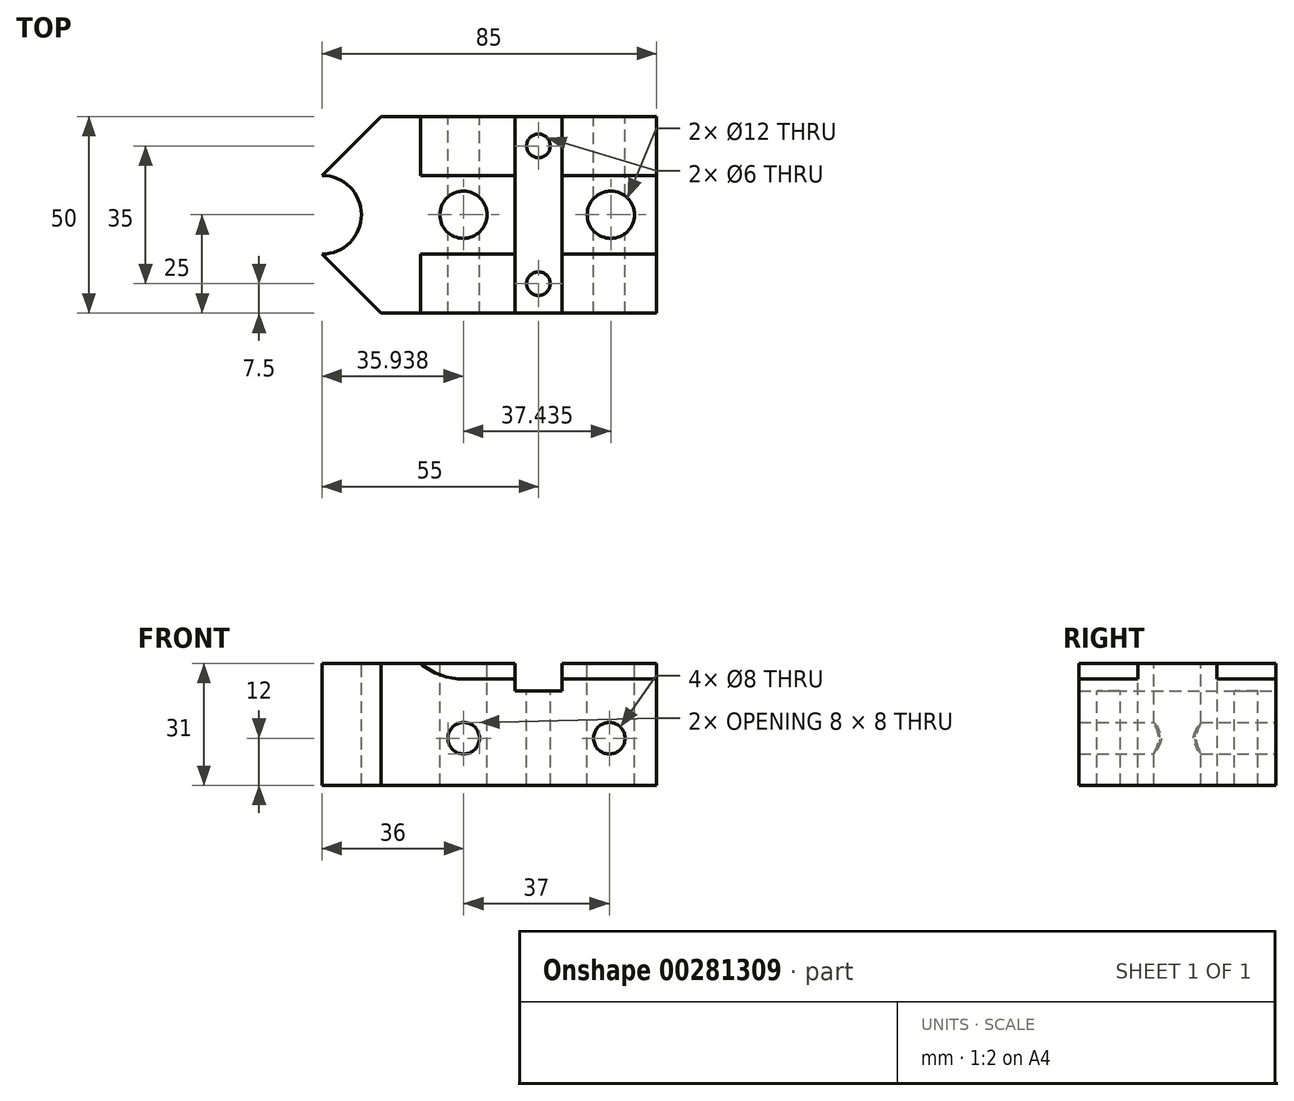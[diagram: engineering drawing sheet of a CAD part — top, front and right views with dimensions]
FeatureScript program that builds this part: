
annotation { "Feature Type Name" : "Feature", "Feature Type Description" : "" }
export const myFeature = defineFeature(function(context is Context, id is Id, definition is map)
    precondition{}
    {
        {
            var Q0;
            Q0=qCreatedBy(makeId("Front.planeOp"),FACE);
            var sketch = newSketch(context, id + "F0", { "sketchPlane" : qUnion([Q0])});
            skLineSegment(sketch, "E0", {"start": v(35, 0) * mm, "end": v(35, 27) * mm});
            skLineSegment(sketch, "E1", {"start": v(35, 27) * mm, "end": v(11, 27) * mm});
            skLineSegment(sketch, "E2", {"start": v(11, 27) * mm, "end": v(11, 24) * mm});
            skLineSegment(sketch, "E3", {"start": v(11, 24) * mm, "end": v(-1, 24) * mm});
            skLineSegment(sketch, "E4", {"start": v(-1, 24) * mm, "end": v(-1, 27) * mm});
            skLineSegment(sketch, "E5", {"start": v(-1, 27) * mm, "end": v(-14, 27) * mm});
            skArc(sketch, "E6", {"start": v(-14, 27) * mm, "mid": v(-19.85, 28.03) * mm, "end": v(-25, 31) * mm});
            skLineSegment(sketch, "E7", {"start": v(-25, 31) * mm, "end": v(-1, 31) * mm});
            skLineSegment(sketch, "E8", {"start": v(-1, 27) * mm, "end": v(-1, 31) * mm});
            skPoint(sketch, "E9.start.orphan", {"position": v(-35, 0) * mm});
            skLineSegment(sketch, "E10", {"start": v(-25, 31) * mm, "end": v(-50, 31) * mm});
            skLineSegment(sketch, "E11", {"start": v(-50, 31) * mm, "end": v(-50, 0) * mm});
            skLineSegment(sketch, "E12", {"start": v(35, 0) * mm, "end": v(-50, 0) * mm});
            skPoint(sketch, "E13.endSnap0", {"position": v(23, 27) * mm});
            skPoint(sketch, "E14.end.orphan", {"position": v(35, 12) * mm});
            skCircle(sketch, "E15", {"center": v(23, 12) * mm, "radius": 4 * mm});
            skCircle(sketch, "E16", {"center": v(-14, 12) * mm, "radius": 4 * mm});
            skSolve(sketch);
        }
        {
            var Q0;
            Q0=makeQuery(id+"F0.imprint","IMPRINT",FACE,{"disambiguationData":[TD([[makeQuery(id+"F0.imprint","IMPRINT",EDGE,{"derivedFrom":sQuery(id+"F0.wireOp",EDGE,"E0")}),1.0]])]});
            extrude(context, id + "F1", {"entities" : qUnion([Q0]), "endBound" : BoundingType.SYMMETRIC, "depth" : 50 * mm});
        }
        {
            var Q0;
            Q0=makeQuery(id+"F0.imprint","IMPRINT",FACE,{"disambiguationData":[TD([[makeQuery(id+"F0.imprint","IMPRINT",EDGE,{"derivedFrom":sQuery(id+"F0.wireOp",EDGE,"E5")}),-1.0]])]});
            extrude(context, id + "F2", {"entities" : qUnion([Q0]), "operationType" : NewBodyOperationType.ADD, "endBound" : BoundingType.SYMMETRIC, "depth" : 20 * mm});
        }
        {
            var Q0;
            Q0=makeQuery(id+"F1.opExtrude","CAP_EDGE",EDGE,{"disambiguationData":[OSD([sQuery(id+"F0.wireOp",EDGE,"E11")])],"isStart":false});
            var Q1;
            Q1=makeQuery(id+"F1.opExtrude","CAP_EDGE",EDGE,{"disambiguationData":[OSD([sQuery(id+"F0.wireOp",EDGE,"E11")])],"isStart":true});
            chamfer(context, id + "F3", {"entities" : qUnion([Q0, Q1]), "width" : 15 * mm, "tangentPropagation" : true});
        }
        {
            var Q0;
            Q0=makeQuery(id+"F2.boolean.opBoolean","MERGE",FACE,{"derivedFrom":[makeQuery(id+"F1.opExtrude","SWEPT_FACE",FACE,{"disambiguationData":[OSD([sQuery(id+"F0.wireOp",EDGE,"E10")])]}),makeQuery(id+"F2.opExtrude","SWEPT_FACE",FACE,{"disambiguationData":[OSD([sQuery(id+"F0.wireOp",EDGE,"E7")])]})]});
            var sketch = newSketch(context, id + "F4", { "sketchPlane" : qUnion([Q0])});
            skCircle(sketch, "E17", {"center": v(-50, 0) * mm, "radius": 10 * mm});
            skSolve(sketch);
        }
        {
            var Q0;
            Q0 = qSketchRegion(id + "F4", true);
            extrude(context, id + "F5", {"entities" : qUnion([Q0]), "operationType" : NewBodyOperationType.REMOVE, "oppositeDirection" : true, "depth" : 31 * mm});
        }
        {
            var Q0;
            Q0=makeQuery(id+"F1.opExtrude","SWEPT_FACE",FACE,{"disambiguationData":[OSD([sQuery(id+"F0.wireOp",EDGE,"E0")])]});
            var sketch = newSketch(context, id + "F6", { "sketchPlane" : qUnion([Q0])});
            skLineSegment(sketch, "E18", {"start": v(-10, 27) * mm, "end": v(-10, 31) * mm});
            skLineSegment(sketch, "E19", {"start": v(-10, 31) * mm, "end": v(10, 31) * mm});
            skLineSegment(sketch, "E20", {"start": v(10, 31) * mm, "end": v(10, 27) * mm});
            skLineSegment(sketch, "E21", {"start": v(10, 27) * mm, "end": v(-10, 27) * mm});
            skSolve(sketch);
        }
        {
            var Q0;
            Q0=makeQuery(id+"F6.imprint","IMPRINT",FACE,{"disambiguationData":[TD([[makeQuery(id+"F6.imprint","IMPRINT",EDGE,{"derivedFrom":sQuery(id+"F6.wireOp",EDGE,"E18")}),-1.0]])]});
            extrude(context, id + "F7", {"entities" : qUnion([Q0]), "operationType" : NewBodyOperationType.ADD, "oppositeDirection" : true, "depth" : 24 * mm});
        }
        {
            var Q0;
            Q0=makeQuery(id+"F2.boolean.opBoolean","MERGE",FACE,{"derivedFrom":[makeQuery(id+"F1.opExtrude","SWEPT_FACE",FACE,{"disambiguationData":[OSD([sQuery(id+"F0.wireOp",EDGE,"E10")])]}),makeQuery(id+"F2.opExtrude","SWEPT_FACE",FACE,{"disambiguationData":[OSD([sQuery(id+"F0.wireOp",EDGE,"E7")])]})]});
            var sketch = newSketch(context, id + "F8", { "sketchPlane" : qUnion([Q0])});
            skCircle(sketch, "E22", {"center": v(-14.06, 0) * mm, "radius": 6 * mm});
            skCircle(sketch, "E23", {"center": v(23.37, 0) * mm, "radius": 6 * mm});
            skSolve(sketch);
        }
        {
            var Q0;
            Q0=makeQuery(id+"F8.imprint","IMPRINT",FACE,{"disambiguationData":[TD([[makeQuery(id+"F8.imprint","IMPRINT",EDGE,{"derivedFrom":sQuery(id+"F8.wireOp",EDGE,"E22")}),1.0]])]});
            var Q1;
            Q1=makeQuery(id+"F8.imprint","IMPRINT",FACE,{"disambiguationData":[TD([[makeQuery(id+"F8.imprint","IMPRINT",EDGE,{"derivedFrom":sQuery(id+"F8.wireOp",EDGE,"E23")}),1.0]])]});
            extrude(context, id + "F9", {"entities" : qUnion([Q0, Q1]), "operationType" : NewBodyOperationType.REMOVE, "oppositeDirection" : true, "depth" : 31 * mm});
        }
        {
            var Q0;
            Q0=makeQuery(id+"F1.opExtrude","SWEPT_FACE",FACE,{"disambiguationData":[OSD([sQuery(id+"F0.wireOp",EDGE,"E3")])]});
            var sketch = newSketch(context, id + "F10", { "sketchPlane" : qUnion([Q0])});
            skPoint(sketch, "E24.endSnap0", {"position": v(5, -25) * mm});
            skCircle(sketch, "E25", {"center": v(5, 17.5) * mm, "radius": 3 * mm});
            skCircle(sketch, "E26", {"center": v(5, -17.5) * mm, "radius": 3 * mm});
            skPoint(sketch, "E27.orphan", {"position": v(5, 25) * mm});
            skPoint(sketch, "E24.start.orphan", {"position": v(5, -25) * mm});
            skSolve(sketch);
        }
        {
            var Q0;
            Q0 = qSketchRegion(id + "F10", true);
            extrude(context, id + "F11", {"entities" : qUnion([Q0]), "operationType" : NewBodyOperationType.REMOVE, "oppositeDirection" : true, "depth" : 27 * mm});
        }
    });
